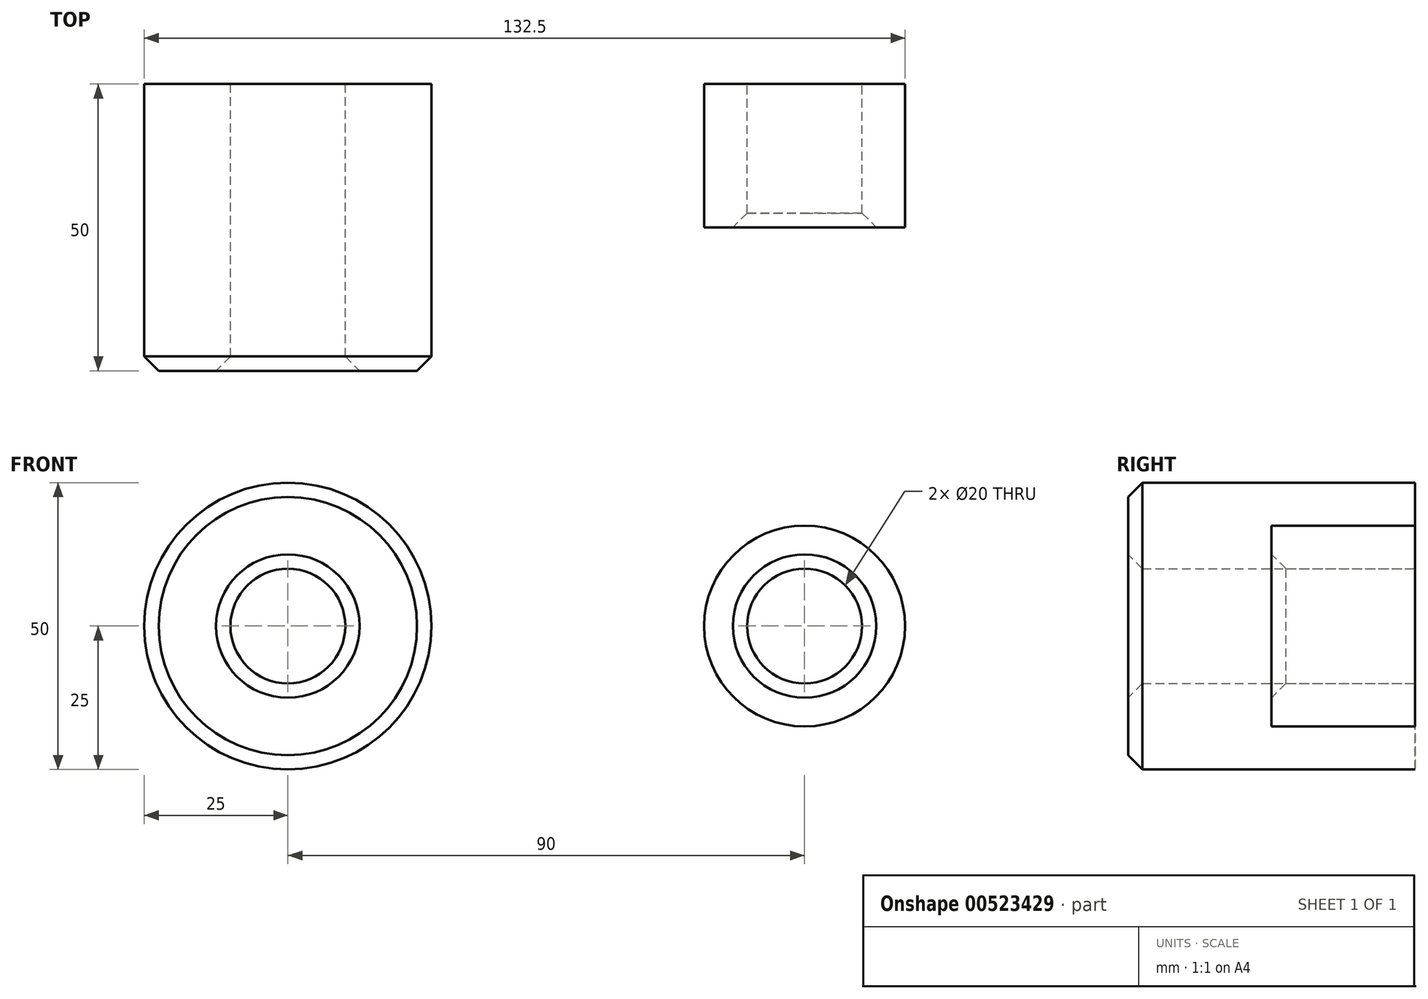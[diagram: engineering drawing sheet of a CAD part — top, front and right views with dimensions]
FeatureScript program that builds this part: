
annotation { "Feature Type Name" : "Feature", "Feature Type Description" : "" }
export const myFeature = defineFeature(function(context is Context, id is Id, definition is map)
    precondition{}
    {
        {
            var Q0;
            Q0=qCreatedBy(makeId("Front.planeOp"),FACE);
            var sketch = newSketch(context, id + "F0", { "sketchPlane" : qUnion([Q0])});
            skCircle(sketch, "E0", {"center": v(0, 0) * mm, "radius": 25 * mm});
            skCircle(sketch, "E1", {"center": v(90, 0) * mm, "radius": 17.5 * mm});
            skLineSegment(sketch, "E2", {"start": v(2.08, 24.91) * mm, "end": v(91.46, 17.44) * mm});
            skLineSegment(sketch, "E3", {"start": v(91.46, 17.44) * mm, "end": v(2.08, 24.91) * mm});
            skLineSegment(sketch, "E4", {"start": v(2.08, -24.91) * mm, "end": v(91.46, -17.44) * mm});
            skCircle(sketch, "E5", {"center": v(0, 0) * mm, "radius": 10 * mm});
            skCircle(sketch, "E6", {"center": v(90, 0) * mm, "radius": 10 * mm});
            skSolve(sketch);
        }
        {
            var Q0;
            {var subQ0=sQuery(id+"F0.wireOp",EDGE,"E3");Q0=makeQuery(id+"F0.imprint","IMPRINT",FACE,{"disambiguationData":[TD([[makeQuery(id+"F0.imprint","IMPRINT",EDGE,{"derivedFrom":subQ0}),1.0]])]});}
            var Q1;
            Q1=makeQuery(id+"F0.imprint","IMPRINT",FACE,{"disambiguationData":[TD([[makeQuery(id+"F0.imprint","IMPRINT",EDGE,{"derivedFrom":sQuery(id+"F0.wireOp",EDGE,"E5")}),-1.0]])]});
            var Q2;
            Q2=makeQuery(id+"F0.imprint","IMPRINT",FACE,{"disambiguationData":[TD([[makeQuery(id+"F0.imprint","IMPRINT",EDGE,{"derivedFrom":sQuery(id+"F0.wireOp",EDGE,"E6")}),-1.0]])]});
            extrude(context, id + "F1", {"entities" : qUnion([Q0, Q1, Q2]), "depth" : 25 * mm, "offsetDistance" : 25 * mm});
        }
        {
            var Q0;
            Q0=makeQuery(id+"F0.imprint","IMPRINT",FACE,{"disambiguationData":[TD([[makeQuery(id+"F0.imprint","IMPRINT",EDGE,{"derivedFrom":sQuery(id+"F0.wireOp",EDGE,"E5")}),-1.0]])]});
            extrude(context, id + "F2", {"entities" : qUnion([Q0]), "operationType" : NewBodyOperationType.ADD, "depth" : 50 * mm, "offsetDistance" : 25 * mm});
        }
        {
            var Q0;
            Q0=makeQuery(id+"F2.opExtrude","CAP_EDGE",EDGE,{"disambiguationData":[OSD([sQuery(id+"F0.wireOp",EDGE,"E0")])],"isStart":false});
            var Q1;
            Q1=makeQuery(id+"F2.opExtrude","CAP_EDGE",EDGE,{"disambiguationData":[OSD([sQuery(id+"F0.wireOp",EDGE,"E5")])],"isStart":false});
            var Q2;
            Q2=makeQuery(id+"F1.opExtrude","CAP_EDGE",EDGE,{"disambiguationData":[OSD([sQuery(id+"F0.wireOp",EDGE,"E6")])],"isStart":false});
            chamfer(context, id + "F3", {"entities" : qUnion([Q0, Q1, Q2]), "width" : 2.5 * mm, "tangentPropagation" : true});
        }
    });
